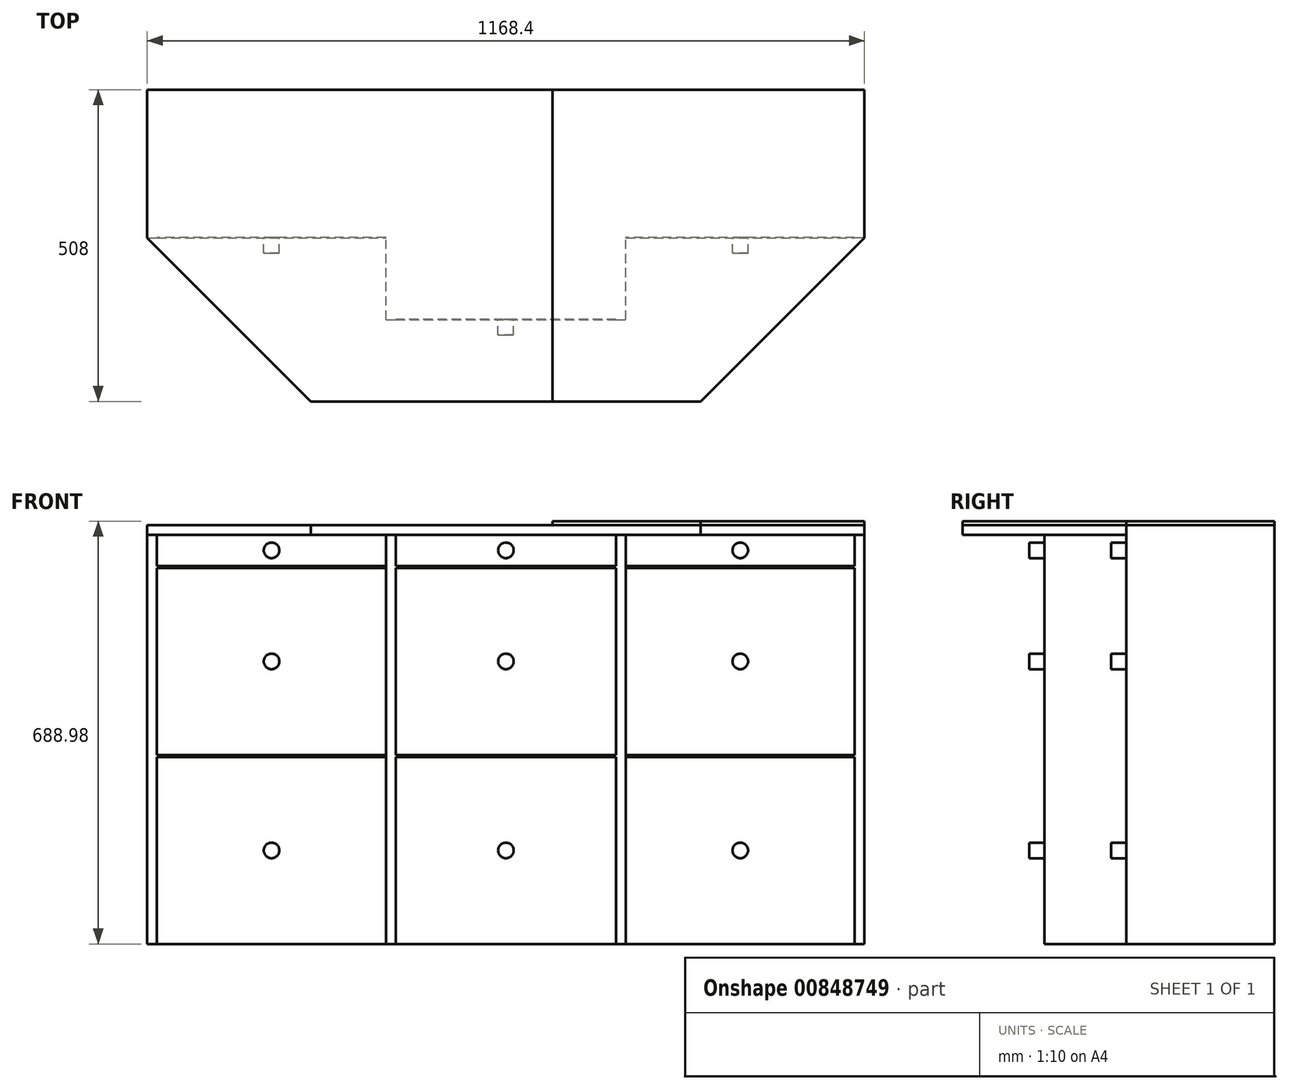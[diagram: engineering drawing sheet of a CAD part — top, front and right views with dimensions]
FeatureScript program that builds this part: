
annotation { "Feature Type Name" : "Feature", "Feature Type Description" : "" }
export const myFeature = defineFeature(function(context is Context, id is Id, definition is map)
    precondition{}
    {
        {
            var Q0;
            Q0=qCreatedBy(makeId("Top.planeOp"),FACE);
            var sketch = newSketch(context, id + "F0", { "sketchPlane" : qUnion([Q0])});
            skLineSegment(sketch, "E0", {"start": v(-584.2, 254) * mm, "end": v(584.2, 254) * mm});
            skLineSegment(sketch, "E1", {"start": v(584.2, 254) * mm, "end": v(584.2, 12.7) * mm});
            skLineSegment(sketch, "E2", {"start": v(-584.2, 254) * mm, "end": v(-584.2, 12.7) * mm});
            skLineSegment(sketch, "E3", {"start": v(-317.5, -254) * mm, "end": v(317.5, -254) * mm});
            skLineSegment(sketch, "E4", {"start": v(584.2, 12.7) * mm, "end": v(317.5, -254) * mm});
            skLineSegment(sketch, "E5", {"start": v(-584.2, 12.7) * mm, "end": v(-317.5, -254) * mm});
            skSolve(sketch);
        }
        {
            var Q0;
            Q0 = qSketchRegion(id + "F0", true);
            extrude(context, id + "F1", {"entities" : qUnion([Q0]), "depth" : 15.88 * mm, "offsetDistance" : 25.4 * mm});
        }
        {
            var Q0;
            Q0=makeQuery(id+"F1.opExtrude","CAP_FACE",FACE,{"disambiguationData":[OSD([sQuery(id+"F0.wireOp",EDGE,"E0"),sQuery(id+"F0.wireOp",EDGE,"E1"),sQuery(id+"F0.wireOp",EDGE,"E2"),sQuery(id+"F0.wireOp",EDGE,"E3"),sQuery(id+"F0.wireOp",EDGE,"E4"),sQuery(id+"F0.wireOp",EDGE,"E5")])],"isStart":true});
            var sketch = newSketch(context, id + "F2", { "sketchPlane" : qUnion([Q0])});
            skLineSegment(sketch, "E6.bottom", {"start": v(-584.2, -12.7) * mm, "end": v(-568.33, -12.7) * mm});
            skLineSegment(sketch, "E6.top", {"start": v(-584.2, -254) * mm, "end": v(-568.33, -254) * mm});
            skLineSegment(sketch, "E6.left", {"start": v(-584.2, -12.7) * mm, "end": v(-584.2, -254) * mm});
            skLineSegment(sketch, "E6.right", {"start": v(-568.33, -12.7) * mm, "end": v(-568.33, -238.13) * mm});
            skLineSegment(sketch, "E7.bottom", {"start": v(584.2, -12.7) * mm, "end": v(568.33, -12.7) * mm});
            skLineSegment(sketch, "E7.top", {"start": v(584.2, -254) * mm, "end": v(568.33, -254) * mm});
            skLineSegment(sketch, "E7.left", {"start": v(584.2, -12.7) * mm, "end": v(584.2, -254) * mm});
            skLineSegment(sketch, "E7.right", {"start": v(568.33, -12.7) * mm, "end": v(568.33, -238.12) * mm});
            skLineSegment(sketch, "E8", {"start": v(-568.33, -254) * mm, "end": v(568.33, -254) * mm});
            skLineSegment(sketch, "E9", {"start": v(568.33, -238.12) * mm, "end": v(-568.33, -238.13) * mm});
            skLineSegment(sketch, "E10", {"start": v(-187.32, -238.13) * mm, "end": v(-187.33, 120.65) * mm, "construction": true});
            skLineSegment(sketch, "E11", {"start": v(187.32, -238.12) * mm, "end": v(187.32, 120.65) * mm, "construction": true});
            skLineSegment(sketch, "E12", {"start": v(187.32, 120.65) * mm, "end": v(195.26, 120.65) * mm});
            skLineSegment(sketch, "E13", {"start": v(187.32, 120.65) * mm, "end": v(179.39, 120.65) * mm});
            skLineSegment(sketch, "E14", {"start": v(-187.33, 120.65) * mm, "end": v(-195.26, 120.65) * mm});
            skLineSegment(sketch, "E15", {"start": v(-187.33, 120.65) * mm, "end": v(-179.39, 120.65) * mm});
            skLineSegment(sketch, "E16", {"start": v(195.26, 120.65) * mm, "end": v(195.26, -238.12) * mm});
            skLineSegment(sketch, "E17", {"start": v(179.39, 120.65) * mm, "end": v(179.39, -238.12) * mm});
            skLineSegment(sketch, "E18", {"start": v(-195.26, 120.65) * mm, "end": v(-195.26, -238.13) * mm});
            skLineSegment(sketch, "E19", {"start": v(-179.39, 120.65) * mm, "end": v(-179.39, -238.13) * mm});
            skLineSegment(sketch, "E20", {"start": v(-450.85, 120.65) * mm, "end": v(450.85, 120.65) * mm, "construction": true});
            skSolve(sketch);
        }
        {
            var Q0;
            Q0 = qSketchRegion(id + "F2", true);
            extrude(context, id + "F3", {"entities" : qUnion([Q0]), "operationType" : NewBodyOperationType.ADD, "depth" : 666.75 * mm, "offsetDistance" : 25.4 * mm});
        }
        {
            var Q0;
            {var subQ0=sQuery(id+"F2.wireOp",EDGE,"E9");Q0=makeQuery(id+"F3.opExtrude","SWEPT_FACE",FACE,{"disambiguationData":[OSD([subQ0]),TDD([makeQuery(id+"F2.imprint","IMPRINT",EDGE,{"disambiguationData":[TD([[makeQuery(id+"F2.imprint","INTERSECT",VERTEX,{"derivedFrom":[sQuery(id+"F2.wireOp",EDGE,"E6.right"),subQ0]}),1.0]])],"derivedFrom":subQ0})])]});}
            var sketch = newSketch(context, id + "F4", { "sketchPlane" : qUnion([Q0])});
            skLineSegment(sketch, "E21.bottom", {"start": v(-568.33, -666.75) * mm, "end": v(-195.26, -666.75) * mm});
            skLineSegment(sketch, "E21.top", {"start": v(-568.33, -361.95) * mm, "end": v(-195.26, -361.95) * mm});
            skLineSegment(sketch, "E21.left", {"start": v(-568.33, -666.75) * mm, "end": v(-568.33, -361.95) * mm});
            skLineSegment(sketch, "E21.right", {"start": v(-195.26, -666.75) * mm, "end": v(-195.26, -361.95) * mm});
            skLineSegment(sketch, "E22.bottom", {"start": v(-568.33, -358.78) * mm, "end": v(-195.26, -358.78) * mm});
            skLineSegment(sketch, "E22.top", {"start": v(-568.33, -53.98) * mm, "end": v(-195.26, -53.98) * mm});
            skLineSegment(sketch, "E22.left", {"start": v(-568.33, -358.78) * mm, "end": v(-568.33, -53.98) * mm});
            skLineSegment(sketch, "E22.right", {"start": v(-195.26, -358.78) * mm, "end": v(-195.26, -53.97) * mm});
            skLineSegment(sketch, "E23.bottom", {"start": v(-568.33, 0) * mm, "end": v(-195.26, 0) * mm});
            skLineSegment(sketch, "E23.top", {"start": v(-568.33, -50.8) * mm, "end": v(-195.26, -50.8) * mm});
            skLineSegment(sketch, "E23.left", {"start": v(-568.33, 0) * mm, "end": v(-568.33, -50.8) * mm});
            skLineSegment(sketch, "E23.right", {"start": v(-195.26, 0) * mm, "end": v(-195.26, -50.8) * mm});
            skSolve(sketch);
        }
        {
            var Q0;
            Q0 = qSketchRegion(id + "F4", true);
            extrude(context, id + "F5", {"entities" : qUnion([Q0]), "operationType" : NewBodyOperationType.ADD, "depth" : 225.3 * mm, "offsetDistance" : 25.4 * mm});
        }
        {
            var Q0;
            {var subQ0=sQuery(id+"F2.wireOp",EDGE,"E9");Q0=makeQuery(id+"F3.opExtrude","SWEPT_FACE",FACE,{"disambiguationData":[OSD([subQ0]),TDD([makeQuery(id+"F2.imprint","IMPRINT",EDGE,{"disambiguationData":[TD([[makeQuery(id+"F2.imprint","INTERSECT",VERTEX,{"derivedFrom":[sQuery(id+"F2.wireOp",EDGE,"E7.right"),subQ0]}),-1.0]])],"derivedFrom":subQ0})])]});}
            var sketch = newSketch(context, id + "F6", { "sketchPlane" : qUnion([Q0])});
            skLineSegment(sketch, "E24.bottom", {"start": v(195.26, -666.75) * mm, "end": v(568.33, -666.75) * mm});
            skLineSegment(sketch, "E24.top", {"start": v(195.26, -361.95) * mm, "end": v(568.33, -361.95) * mm});
            skLineSegment(sketch, "E24.left", {"start": v(195.26, -666.75) * mm, "end": v(195.26, -361.95) * mm});
            skLineSegment(sketch, "E24.right", {"start": v(568.33, -666.75) * mm, "end": v(568.33, -361.95) * mm});
            skLineSegment(sketch, "E25.bottom", {"start": v(195.26, -358.78) * mm, "end": v(568.33, -358.78) * mm});
            skLineSegment(sketch, "E25.top", {"start": v(195.26, -53.98) * mm, "end": v(568.33, -53.98) * mm});
            skLineSegment(sketch, "E25.left", {"start": v(195.26, -358.78) * mm, "end": v(195.26, -53.98) * mm});
            skLineSegment(sketch, "E25.right", {"start": v(568.33, -358.78) * mm, "end": v(568.33, -53.97) * mm});
            skLineSegment(sketch, "E26.bottom", {"start": v(195.26, 0) * mm, "end": v(568.33, 0) * mm});
            skLineSegment(sketch, "E26.top", {"start": v(195.26, -50.8) * mm, "end": v(568.33, -50.8) * mm});
            skLineSegment(sketch, "E26.left", {"start": v(195.26, 0) * mm, "end": v(195.26, -50.8) * mm});
            skLineSegment(sketch, "E26.right", {"start": v(568.33, 0) * mm, "end": v(568.33, -50.8) * mm});
            skSolve(sketch);
        }
        {
            var Q0;
            Q0 = qSketchRegion(id + "F6", true);
            extrude(context, id + "F7", {"entities" : qUnion([Q0]), "operationType" : NewBodyOperationType.ADD, "depth" : 225.3 * mm, "offsetDistance" : 25.4 * mm});
        }
        {
            var Q0;
            {var subQ0=sQuery(id+"F2.wireOp",EDGE,"E9");Q0=makeQuery(id+"F3.opExtrude","SWEPT_FACE",FACE,{"disambiguationData":[OSD([subQ0]),TDD([makeQuery(id+"F2.imprint","IMPRINT",EDGE,{"disambiguationData":[TD([[makeQuery(id+"F2.imprint","INTERSECT",VERTEX,{"derivedFrom":[subQ0,sQuery(id+"F2.wireOp",EDGE,"E17")]}),-1.0]])],"derivedFrom":subQ0})])]});}
            var sketch = newSketch(context, id + "F8", { "sketchPlane" : qUnion([Q0])});
            skLineSegment(sketch, "E27.bottom", {"start": v(-179.39, -666.75) * mm, "end": v(179.39, -666.75) * mm});
            skLineSegment(sketch, "E27.top", {"start": v(-179.39, -361.95) * mm, "end": v(179.39, -361.95) * mm});
            skLineSegment(sketch, "E27.left", {"start": v(-179.39, -666.75) * mm, "end": v(-179.39, -361.95) * mm});
            skLineSegment(sketch, "E27.right", {"start": v(179.39, -666.75) * mm, "end": v(179.39, -361.95) * mm});
            skLineSegment(sketch, "E28.bottom", {"start": v(-179.39, -358.78) * mm, "end": v(179.39, -358.78) * mm});
            skLineSegment(sketch, "E28.top", {"start": v(-179.39, -53.98) * mm, "end": v(179.39, -53.98) * mm});
            skLineSegment(sketch, "E28.left", {"start": v(-179.39, -358.78) * mm, "end": v(-179.39, -53.98) * mm});
            skLineSegment(sketch, "E28.right", {"start": v(179.39, -358.78) * mm, "end": v(179.39, -53.97) * mm});
            skLineSegment(sketch, "E29.bottom", {"start": v(-179.39, 0) * mm, "end": v(179.39, 0) * mm});
            skLineSegment(sketch, "E29.top", {"start": v(-179.39, -50.8) * mm, "end": v(179.39, -50.8) * mm});
            skLineSegment(sketch, "E29.left", {"start": v(-179.39, 0) * mm, "end": v(-179.39, -50.8) * mm});
            skLineSegment(sketch, "E29.right", {"start": v(179.39, 0) * mm, "end": v(179.39, -50.8) * mm});
            skSolve(sketch);
        }
        {
            var Q0;
            Q0 = qSketchRegion(id + "F8", true);
            extrude(context, id + "F9", {"entities" : qUnion([Q0]), "operationType" : NewBodyOperationType.ADD, "depth" : 358.65 * mm, "offsetDistance" : 25.4 * mm});
        }
        {
            var Q0;
            Q0=makeQuery(id+"F5.opExtrude","CAP_FACE",FACE,{"disambiguationData":[OSD([sQuery(id+"F4.wireOp",EDGE,"E21.bottom"),sQuery(id+"F4.wireOp",EDGE,"E21.top"),sQuery(id+"F4.wireOp",EDGE,"E21.left"),sQuery(id+"F4.wireOp",EDGE,"E21.right")])],"isStart":false});
            var sketch = newSketch(context, id + "F10", { "sketchPlane" : qUnion([Q0])});
            skLineSegment(sketch, "E30", {"start": v(-381.8, -361.95) * mm, "end": v(-381.8, -666.75) * mm, "construction": true});
            skLineSegment(sketch, "E31", {"start": v(-195.26, -514.35) * mm, "end": v(-568.33, -514.35) * mm, "construction": true});
            skCircle(sketch, "E32", {"center": v(-381.8, -514.35) * mm, "radius": 12.7 * mm});
            skSolve(sketch);
        }
        {
            var Q0;
            Q0 = qSketchRegion(id + "F10", true);
            extrude(context, id + "F11", {"entities" : qUnion([Q0]), "operationType" : NewBodyOperationType.ADD, "depth" : 25.4 * mm, "offsetDistance" : 25.4 * mm});
        }
        {
            var Q0;
            Q0=makeQuery(id+"F5.opExtrude","CAP_FACE",FACE,{"disambiguationData":[OSD([sQuery(id+"F4.wireOp",EDGE,"E22.bottom"),sQuery(id+"F4.wireOp",EDGE,"E22.top"),sQuery(id+"F4.wireOp",EDGE,"E22.left"),sQuery(id+"F4.wireOp",EDGE,"E22.right")])],"isStart":false});
            var sketch = newSketch(context, id + "F12", { "sketchPlane" : qUnion([Q0])});
            skLineSegment(sketch, "E33", {"start": v(-568.33, -206.38) * mm, "end": v(-195.26, -206.38) * mm, "construction": true});
            skLineSegment(sketch, "E34", {"start": v(-381.8, -53.98) * mm, "end": v(-381.8, -358.78) * mm, "construction": true});
            skCircle(sketch, "E35", {"center": v(-381.8, -206.38) * mm, "radius": 12.7 * mm});
            skSolve(sketch);
        }
        {
            var Q0;
            Q0 = qSketchRegion(id + "F12", true);
            extrude(context, id + "F13", {"entities" : qUnion([Q0]), "operationType" : NewBodyOperationType.ADD, "depth" : 25.4 * mm, "offsetDistance" : 25.4 * mm});
        }
        {
            var Q0;
            Q0=makeQuery(id+"F5.opExtrude","CAP_FACE",FACE,{"disambiguationData":[OSD([sQuery(id+"F4.wireOp",EDGE,"E23.bottom"),sQuery(id+"F4.wireOp",EDGE,"E23.top"),sQuery(id+"F4.wireOp",EDGE,"E23.left"),sQuery(id+"F4.wireOp",EDGE,"E23.right")])],"isStart":false});
            var sketch = newSketch(context, id + "F14", { "sketchPlane" : qUnion([Q0])});
            skLineSegment(sketch, "E36", {"start": v(-568.33, -25.4) * mm, "end": v(-195.26, -25.4) * mm, "construction": true});
            skLineSegment(sketch, "E37", {"start": v(-381.8, -50.8) * mm, "end": v(-381.8, 0) * mm, "construction": true});
            skCircle(sketch, "E38", {"center": v(-381.8, -25.4) * mm, "radius": 12.7 * mm});
            skSolve(sketch);
        }
        {
            var Q0;
            Q0 = qSketchRegion(id + "F14", true);
            extrude(context, id + "F15", {"entities" : qUnion([Q0]), "operationType" : NewBodyOperationType.ADD, "depth" : 25.4 * mm, "offsetDistance" : 25.4 * mm});
        }
        {
            var Q0;
            Q0=makeQuery(id+"F9.opExtrude","CAP_FACE",FACE,{"disambiguationData":[OSD([sQuery(id+"F8.wireOp",EDGE,"E27.bottom"),sQuery(id+"F8.wireOp",EDGE,"E27.top"),sQuery(id+"F8.wireOp",EDGE,"E27.left"),sQuery(id+"F8.wireOp",EDGE,"E27.right")])],"isStart":false});
            var sketch = newSketch(context, id + "F16", { "sketchPlane" : qUnion([Q0])});
            skLineSegment(sketch, "E39", {"start": v(-179.39, -514.35) * mm, "end": v(179.39, -514.35) * mm, "construction": true});
            skLineSegment(sketch, "E40", {"start": v(0, -361.95) * mm, "end": v(0, -666.75) * mm, "construction": true});
            skCircle(sketch, "E41", {"center": v(0, -514.35) * mm, "radius": 12.7 * mm});
            skSolve(sketch);
        }
        {
            var Q0;
            Q0 = qSketchRegion(id + "F16", true);
            extrude(context, id + "F17", {"entities" : qUnion([Q0]), "operationType" : NewBodyOperationType.ADD, "depth" : 25.4 * mm, "offsetDistance" : 25.4 * mm});
        }
        {
            var Q0;
            Q0=makeQuery(id+"F9.opExtrude","CAP_FACE",FACE,{"disambiguationData":[OSD([sQuery(id+"F8.wireOp",EDGE,"E28.bottom"),sQuery(id+"F8.wireOp",EDGE,"E28.top"),sQuery(id+"F8.wireOp",EDGE,"E28.left"),sQuery(id+"F8.wireOp",EDGE,"E28.right")])],"isStart":false});
            var sketch = newSketch(context, id + "F18", { "sketchPlane" : qUnion([Q0])});
            skLineSegment(sketch, "E42", {"start": v(-179.39, -206.38) * mm, "end": v(179.39, -206.38) * mm, "construction": true});
            skLineSegment(sketch, "E43", {"start": v(0, -53.98) * mm, "end": v(0, -358.78) * mm, "construction": true});
            skCircle(sketch, "E44", {"center": v(0, -206.38) * mm, "radius": 12.7 * mm});
            skSolve(sketch);
        }
        {
            var Q0;
            Q0 = qSketchRegion(id + "F18", true);
            extrude(context, id + "F19", {"entities" : qUnion([Q0]), "operationType" : NewBodyOperationType.ADD, "depth" : 25.4 * mm, "offsetDistance" : 25.4 * mm});
        }
        {
            var Q0;
            Q0=makeQuery(id+"F9.opExtrude","CAP_FACE",FACE,{"disambiguationData":[OSD([sQuery(id+"F8.wireOp",EDGE,"E29.bottom"),sQuery(id+"F8.wireOp",EDGE,"E29.top"),sQuery(id+"F8.wireOp",EDGE,"E29.left"),sQuery(id+"F8.wireOp",EDGE,"E29.right")])],"isStart":false});
            var sketch = newSketch(context, id + "F20", { "sketchPlane" : qUnion([Q0])});
            skLineSegment(sketch, "E45", {"start": v(179.39, -25.4) * mm, "end": v(-179.39, -25.4) * mm, "construction": true});
            skLineSegment(sketch, "E46", {"start": v(0, -50.8) * mm, "end": v(0, 0) * mm, "construction": true});
            skCircle(sketch, "E47", {"center": v(0, -25.4) * mm, "radius": 12.7 * mm});
            skSolve(sketch);
        }
        {
            var Q0;
            Q0 = qSketchRegion(id + "F20", true);
            extrude(context, id + "F21", {"entities" : qUnion([Q0]), "operationType" : NewBodyOperationType.ADD, "depth" : 25.4 * mm, "offsetDistance" : 25.4 * mm});
        }
        {
            var Q0;
            Q0=makeQuery(id+"F7.opExtrude","CAP_FACE",FACE,{"disambiguationData":[OSD([sQuery(id+"F6.wireOp",EDGE,"E24.bottom"),sQuery(id+"F6.wireOp",EDGE,"E24.top"),sQuery(id+"F6.wireOp",EDGE,"E24.left"),sQuery(id+"F6.wireOp",EDGE,"E24.right")])],"isStart":false});
            var sketch = newSketch(context, id + "F22", { "sketchPlane" : qUnion([Q0])});
            skLineSegment(sketch, "E48", {"start": v(568.33, -514.35) * mm, "end": v(195.26, -514.35) * mm, "construction": true});
            skLineSegment(sketch, "E49", {"start": v(381.8, -361.95) * mm, "end": v(381.8, -666.75) * mm, "construction": true});
            skCircle(sketch, "E50", {"center": v(381.8, -514.35) * mm, "radius": 12.7 * mm});
            skSolve(sketch);
        }
        {
            var Q0;
            Q0 = qSketchRegion(id + "F22", true);
            extrude(context, id + "F23", {"entities" : qUnion([Q0]), "operationType" : NewBodyOperationType.ADD, "depth" : 25.4 * mm, "offsetDistance" : 25.4 * mm});
        }
        {
            var Q0;
            Q0=makeQuery(id+"F7.opExtrude","CAP_FACE",FACE,{"disambiguationData":[OSD([sQuery(id+"F6.wireOp",EDGE,"E25.bottom"),sQuery(id+"F6.wireOp",EDGE,"E25.top"),sQuery(id+"F6.wireOp",EDGE,"E25.left"),sQuery(id+"F6.wireOp",EDGE,"E25.right")])],"isStart":false});
            var sketch = newSketch(context, id + "F24", { "sketchPlane" : qUnion([Q0])});
            skLineSegment(sketch, "E51", {"start": v(195.26, -206.38) * mm, "end": v(568.33, -206.38) * mm, "construction": true});
            skLineSegment(sketch, "E52", {"start": v(381.8, -53.98) * mm, "end": v(381.8, -358.78) * mm, "construction": true});
            skCircle(sketch, "E53", {"center": v(381.8, -206.38) * mm, "radius": 12.7 * mm});
            skSolve(sketch);
        }
        {
            var Q0;
            Q0 = qSketchRegion(id + "F24", true);
            extrude(context, id + "F25", {"entities" : qUnion([Q0]), "operationType" : NewBodyOperationType.ADD, "depth" : 25.4 * mm, "offsetDistance" : 25.4 * mm});
        }
        {
            var Q0;
            Q0=makeQuery(id+"F7.opExtrude","CAP_FACE",FACE,{"disambiguationData":[OSD([sQuery(id+"F6.wireOp",EDGE,"E26.bottom"),sQuery(id+"F6.wireOp",EDGE,"E26.top"),sQuery(id+"F6.wireOp",EDGE,"E26.left"),sQuery(id+"F6.wireOp",EDGE,"E26.right")])],"isStart":false});
            var sketch = newSketch(context, id + "F26", { "sketchPlane" : qUnion([Q0])});
            skLineSegment(sketch, "E54", {"start": v(568.33, -25.4) * mm, "end": v(195.26, -25.4) * mm, "construction": true});
            skLineSegment(sketch, "E55", {"start": v(381.8, -50.8) * mm, "end": v(381.8, 0) * mm, "construction": true});
            skCircle(sketch, "E56", {"center": v(381.8, -25.4) * mm, "radius": 12.7 * mm});
            skSolve(sketch);
        }
        {
            var Q0;
            Q0 = qSketchRegion(id + "F26", true);
            extrude(context, id + "F27", {"entities" : qUnion([Q0]), "operationType" : NewBodyOperationType.ADD, "depth" : 25.4 * mm, "offsetDistance" : 25.4 * mm});
        }
        {
            var Q0;
            Q0=makeQuery(id+"F1.opExtrude","CAP_FACE",FACE,{"disambiguationData":[OSD([sQuery(id+"F0.wireOp",EDGE,"E0"),sQuery(id+"F0.wireOp",EDGE,"E1"),sQuery(id+"F0.wireOp",EDGE,"E2"),sQuery(id+"F0.wireOp",EDGE,"E3"),sQuery(id+"F0.wireOp",EDGE,"E4"),sQuery(id+"F0.wireOp",EDGE,"E5")])],"isStart":false});
            var sketch = newSketch(context, id + "F28", { "sketchPlane" : qUnion([Q0])});
            skLineSegment(sketch, "E57", {"start": v(584.2, 254) * mm, "end": v(76.2, 254) * mm});
            skLineSegment(sketch, "E58", {"start": v(76.2, 254) * mm, "end": v(76.2, -254) * mm});
            skLineSegment(sketch, "E59", {"start": v(76.2, -254) * mm, "end": v(317.5, -254) * mm});
            skLineSegment(sketch, "E60", {"start": v(317.5, -254) * mm, "end": v(584.2, 12.7) * mm});
            skLineSegment(sketch, "E61", {"start": v(584.2, 12.7) * mm, "end": v(584.2, 254) * mm});
            skSolve(sketch);
        }
        {
            var Q0;
            Q0 = qSketchRegion(id + "F28", true);
            extrude(context, id + "F29", {"entities" : qUnion([Q0]), "depth" : 6.35 * mm, "offsetDistance" : 25.4 * mm});
        }
        {
            var Q0;
            {var subQ0=sQuery(id+"F2.wireOp",EDGE,"E17");var subQ2=sQuery(id+"F2.wireOp",EDGE,"E9");Q0=makeQuery(id+"F9.boolean.opBoolean","SPLIT",FACE,{"disambiguationData":[TD([makeQuery(id+"F9.opExtrude","SWEPT_FACE",FACE,{"disambiguationData":[OSD([sQuery(id+"F8.wireOp",EDGE,"E27.top")])]})])],"derivedFrom":makeQuery(id+"F3.opExtrude","SWEPT_FACE",FACE,{"disambiguationData":[OSD([subQ2]),TDD([makeQuery(id+"F2.imprint","IMPRINT",EDGE,{"disambiguationData":[TD([[makeQuery(id+"F2.imprint","INTERSECT",VERTEX,{"derivedFrom":[subQ2,subQ0]}),-1.0]])],"derivedFrom":subQ2})])]})});}
            var sketch = newSketch(context, id + "F30", { "sketchPlane" : qUnion([Q0])});
            skLineSegment(sketch, "E62.0", {"start": v(179.39, -358.78) * mm, "end": v(-179.39, -358.78) * mm});
            skLineSegment(sketch, "E62.1", {"start": v(179.39, -361.95) * mm, "end": v(179.39, -358.78) * mm});
            skLineSegment(sketch, "E62.2", {"start": v(-179.39, -361.95) * mm, "end": v(179.39, -361.95) * mm});
            skLineSegment(sketch, "E62.3", {"start": v(-179.39, -358.78) * mm, "end": v(-179.39, -361.95) * mm});
            skSolve(sketch);
        }
        {
            var Q0;
            Q0 = qSketchRegion(id + "F30", true);
            extrude(context, id + "F31", {"entities" : qUnion([Q0]), "operationType" : NewBodyOperationType.ADD, "depth" : 358.77 * mm, "offsetDistance" : 25.4 * mm});
        }
        {
            var Q0;
            {var subQ0=sQuery(id+"F2.wireOp",EDGE,"E17");var subQ2=sQuery(id+"F2.wireOp",EDGE,"E9");Q0=makeQuery(id+"F9.boolean.opBoolean","SPLIT",FACE,{"disambiguationData":[TD([makeQuery(id+"F9.opExtrude","SWEPT_FACE",FACE,{"disambiguationData":[OSD([sQuery(id+"F8.wireOp",EDGE,"E28.top")])]})])],"derivedFrom":makeQuery(id+"F3.opExtrude","SWEPT_FACE",FACE,{"disambiguationData":[OSD([subQ2]),TDD([makeQuery(id+"F2.imprint","IMPRINT",EDGE,{"disambiguationData":[TD([[makeQuery(id+"F2.imprint","INTERSECT",VERTEX,{"derivedFrom":[subQ2,subQ0]}),-1.0]])],"derivedFrom":subQ2})])]})});}
            var sketch = newSketch(context, id + "F32", { "sketchPlane" : qUnion([Q0])});
            skLineSegment(sketch, "E63.0", {"start": v(179.39, -50.8) * mm, "end": v(-179.39, -50.8) * mm});
            skLineSegment(sketch, "E63.1", {"start": v(179.39, -53.97) * mm, "end": v(179.39, -50.8) * mm});
            skLineSegment(sketch, "E63.2", {"start": v(-179.39, -53.98) * mm, "end": v(179.39, -53.98) * mm});
            skLineSegment(sketch, "E63.3", {"start": v(-179.39, -50.8) * mm, "end": v(-179.39, -53.97) * mm});
            skSolve(sketch);
        }
        {
            var Q0;
            Q0 = qSketchRegion(id + "F32", true);
            extrude(context, id + "F33", {"entities" : qUnion([Q0]), "operationType" : NewBodyOperationType.ADD, "depth" : 358.77 * mm, "offsetDistance" : 25.4 * mm});
        }
        {
            var Q0;
            {var subQ0=sQuery(id+"F2.wireOp",EDGE,"E6.right");var subQ2=sQuery(id+"F2.wireOp",EDGE,"E9");Q0=makeQuery(id+"F5.boolean.opBoolean","SPLIT",FACE,{"disambiguationData":[TD([makeQuery(id+"F5.opExtrude","SWEPT_FACE",FACE,{"disambiguationData":[OSD([sQuery(id+"F4.wireOp",EDGE,"E21.top")])]})])],"derivedFrom":makeQuery(id+"F3.opExtrude","SWEPT_FACE",FACE,{"disambiguationData":[OSD([subQ2]),TDD([makeQuery(id+"F2.imprint","IMPRINT",EDGE,{"disambiguationData":[TD([[makeQuery(id+"F2.imprint","INTERSECT",VERTEX,{"derivedFrom":[subQ0,subQ2]}),1.0]])],"derivedFrom":subQ2})])]})});}
            var sketch = newSketch(context, id + "F34", { "sketchPlane" : qUnion([Q0])});
            skLineSegment(sketch, "E64.0", {"start": v(-195.26, -358.78) * mm, "end": v(-568.33, -358.78) * mm});
            skLineSegment(sketch, "E64.1", {"start": v(-195.26, -361.95) * mm, "end": v(-195.26, -358.78) * mm});
            skLineSegment(sketch, "E64.2", {"start": v(-568.33, -361.95) * mm, "end": v(-195.26, -361.95) * mm});
            skLineSegment(sketch, "E64.3", {"start": v(-568.33, -358.78) * mm, "end": v(-568.33, -361.95) * mm});
            skSolve(sketch);
        }
        {
            var Q0;
            Q0 = qSketchRegion(id + "F34", true);
            extrude(context, id + "F35", {"entities" : qUnion([Q0]), "operationType" : NewBodyOperationType.ADD, "depth" : 225.42 * mm, "offsetDistance" : 25.4 * mm});
        }
        {
            var Q0;
            {var subQ0=sQuery(id+"F2.wireOp",EDGE,"E6.right");var subQ2=sQuery(id+"F2.wireOp",EDGE,"E9");Q0=makeQuery(id+"F5.boolean.opBoolean","SPLIT",FACE,{"disambiguationData":[TD([makeQuery(id+"F5.opExtrude","SWEPT_FACE",FACE,{"disambiguationData":[OSD([sQuery(id+"F4.wireOp",EDGE,"E22.top")])]})])],"derivedFrom":makeQuery(id+"F3.opExtrude","SWEPT_FACE",FACE,{"disambiguationData":[OSD([subQ2]),TDD([makeQuery(id+"F2.imprint","IMPRINT",EDGE,{"disambiguationData":[TD([[makeQuery(id+"F2.imprint","INTERSECT",VERTEX,{"derivedFrom":[subQ0,subQ2]}),1.0]])],"derivedFrom":subQ2})])]})});}
            var sketch = newSketch(context, id + "F36", { "sketchPlane" : qUnion([Q0])});
            skLineSegment(sketch, "E65.0", {"start": v(-195.26, -50.8) * mm, "end": v(-568.33, -50.8) * mm});
            skLineSegment(sketch, "E65.1", {"start": v(-195.26, -53.97) * mm, "end": v(-195.26, -50.8) * mm});
            skLineSegment(sketch, "E65.2", {"start": v(-568.33, -53.98) * mm, "end": v(-195.26, -53.98) * mm});
            skLineSegment(sketch, "E65.3", {"start": v(-568.33, -50.8) * mm, "end": v(-568.33, -53.97) * mm});
            skSolve(sketch);
        }
        {
            var Q0;
            Q0 = qSketchRegion(id + "F36", true);
            extrude(context, id + "F37", {"entities" : qUnion([Q0]), "operationType" : NewBodyOperationType.ADD, "depth" : 225.42 * mm, "offsetDistance" : 25.4 * mm});
        }
        {
            var Q0;
            {var subQ0=sQuery(id+"F2.wireOp",EDGE,"E7.right");var subQ2=sQuery(id+"F2.wireOp",EDGE,"E9");Q0=makeQuery(id+"F7.boolean.opBoolean","SPLIT",FACE,{"disambiguationData":[TD([makeQuery(id+"F7.opExtrude","SWEPT_FACE",FACE,{"disambiguationData":[OSD([sQuery(id+"F6.wireOp",EDGE,"E25.top")])]})])],"derivedFrom":makeQuery(id+"F3.opExtrude","SWEPT_FACE",FACE,{"disambiguationData":[OSD([subQ2]),TDD([makeQuery(id+"F2.imprint","IMPRINT",EDGE,{"disambiguationData":[TD([[makeQuery(id+"F2.imprint","INTERSECT",VERTEX,{"derivedFrom":[subQ0,subQ2]}),-1.0]])],"derivedFrom":subQ2})])]})});}
            var sketch = newSketch(context, id + "F38", { "sketchPlane" : qUnion([Q0])});
            skLineSegment(sketch, "E66.0", {"start": v(568.33, -50.8) * mm, "end": v(195.26, -50.8) * mm});
            skLineSegment(sketch, "E66.1", {"start": v(568.33, -53.97) * mm, "end": v(568.33, -50.8) * mm});
            skLineSegment(sketch, "E66.2", {"start": v(195.26, -53.98) * mm, "end": v(568.33, -53.98) * mm});
            skLineSegment(sketch, "E66.3", {"start": v(195.26, -50.8) * mm, "end": v(195.26, -53.97) * mm});
            skSolve(sketch);
        }
        {
            var Q0;
            Q0 = qSketchRegion(id + "F38", true);
            extrude(context, id + "F39", {"entities" : qUnion([Q0]), "operationType" : NewBodyOperationType.ADD, "depth" : 225.42 * mm, "offsetDistance" : 25.4 * mm});
        }
        {
            var Q0;
            {var subQ0=sQuery(id+"F2.wireOp",EDGE,"E7.right");var subQ2=sQuery(id+"F2.wireOp",EDGE,"E9");Q0=makeQuery(id+"F7.boolean.opBoolean","SPLIT",FACE,{"disambiguationData":[TD([makeQuery(id+"F7.opExtrude","SWEPT_FACE",FACE,{"disambiguationData":[OSD([sQuery(id+"F6.wireOp",EDGE,"E24.top")])]})])],"derivedFrom":makeQuery(id+"F3.opExtrude","SWEPT_FACE",FACE,{"disambiguationData":[OSD([subQ2]),TDD([makeQuery(id+"F2.imprint","IMPRINT",EDGE,{"disambiguationData":[TD([[makeQuery(id+"F2.imprint","INTERSECT",VERTEX,{"derivedFrom":[subQ0,subQ2]}),-1.0]])],"derivedFrom":subQ2})])]})});}
            var sketch = newSketch(context, id + "F40", { "sketchPlane" : qUnion([Q0])});
            skLineSegment(sketch, "E67.0", {"start": v(568.33, -358.78) * mm, "end": v(195.26, -358.78) * mm});
            skLineSegment(sketch, "E67.1", {"start": v(568.33, -361.95) * mm, "end": v(568.33, -358.78) * mm});
            skLineSegment(sketch, "E67.2", {"start": v(195.26, -361.95) * mm, "end": v(568.33, -361.95) * mm});
            skLineSegment(sketch, "E67.3", {"start": v(195.26, -358.78) * mm, "end": v(195.26, -361.95) * mm});
            skSolve(sketch);
        }
        {
            var Q0;
            Q0 = qSketchRegion(id + "F40", true);
            extrude(context, id + "F41", {"entities" : qUnion([Q0]), "operationType" : NewBodyOperationType.ADD, "depth" : 225.42 * mm, "offsetDistance" : 25.4 * mm});
        }
    });
